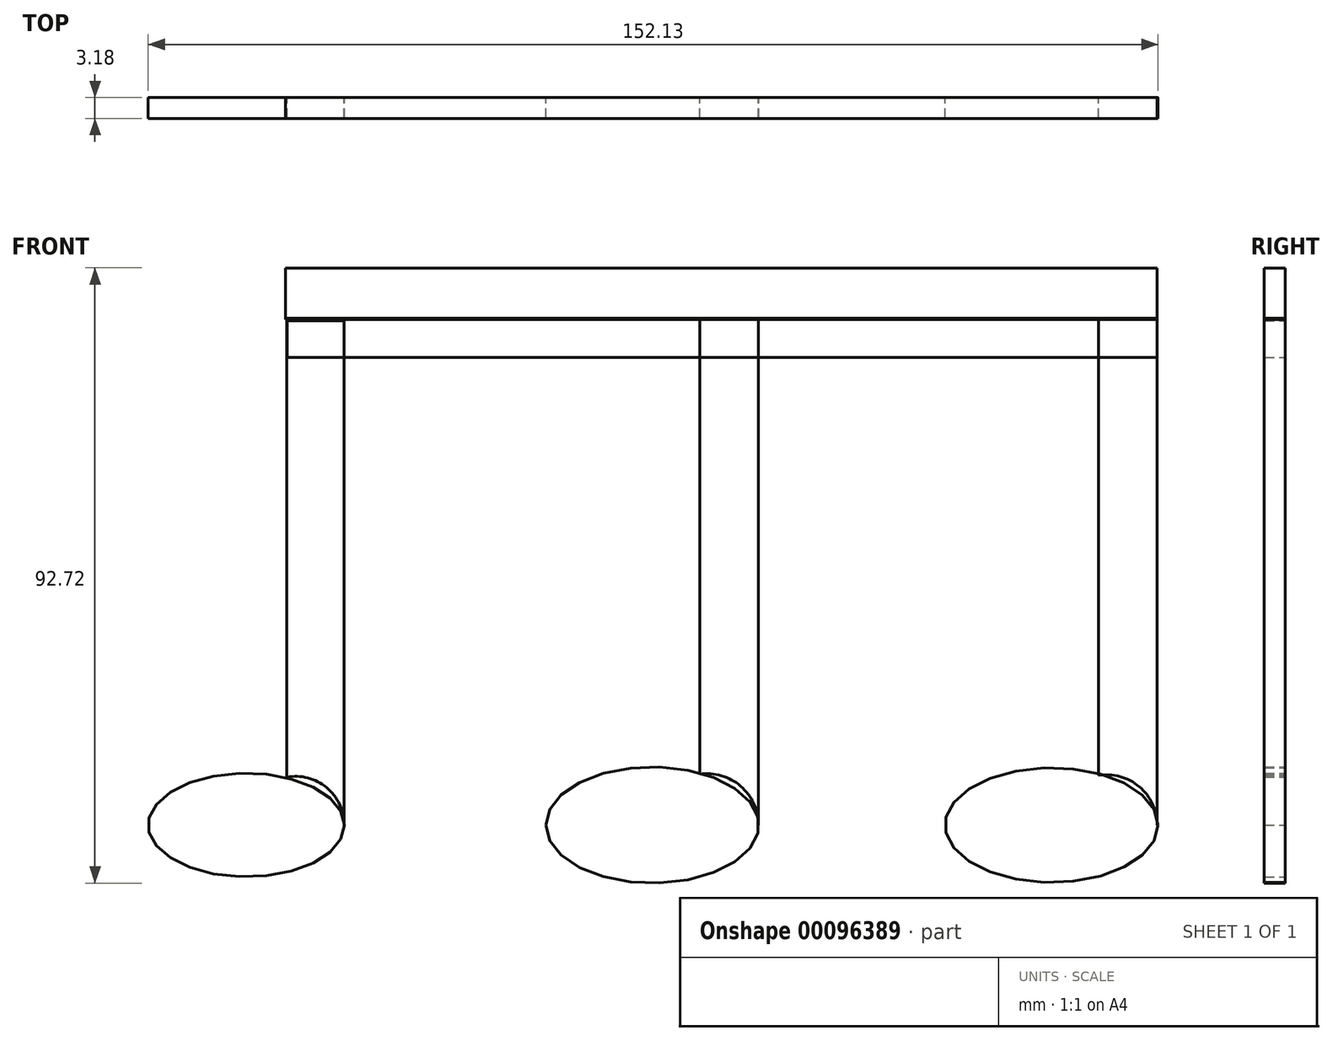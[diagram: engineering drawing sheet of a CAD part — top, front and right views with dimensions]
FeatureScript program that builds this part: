
annotation { "Feature Type Name" : "Feature", "Feature Type Description" : "" }
export const myFeature = defineFeature(function(context is Context, id is Id, definition is map)
    precondition{}
    {
        {
            var Q0;
            Q0=qCreatedBy(makeId("Front.planeOp"),FACE);
            var sketch = newSketch(context, id + "F0", { "sketchPlane" : qUnion([Q0])});
            skEllipse(sketch, "E0", {"center": v(-61.15, 0) * mm, "majorRadius": 14.79 * mm, "minorRadius": 7.8 * mm, "majorAxis": v(1, 0)});
            skSolve(sketch);
        }
        {
            var Q0;
            Q0=qCreatedBy(makeId("Front.planeOp"),FACE);
            var sketch = newSketch(context, id + "F1", { "sketchPlane" : qUnion([Q0])});
            skEllipse(sketch, "E1", {"center": v(60.15, 0) * mm, "majorRadius": 16.04 * mm, "minorRadius": 8.64 * mm, "majorAxis": v(1, 0)});
            skSolve(sketch);
        }
        {
            var Q0;
            Q0=qCreatedBy(makeId("Front.planeOp"),FACE);
            var sketch = newSketch(context, id + "F2", { "sketchPlane" : qUnion([Q0])});
            skEllipse(sketch, "E2", {"center": v(0, 0) * mm, "majorRadius": 16.04 * mm, "minorRadius": 8.75 * mm, "majorAxis": v(-1, 0)});
            skSolve(sketch);
        }
        {
            var Q0;
            Q0=qCreatedBy(makeId("Front.planeOp"),FACE);
            var sketch = newSketch(context, id + "F3", { "sketchPlane" : qUnion([Q0])});
            skLineSegment(sketch, "E3", {"start": v(-46.4, 0) * mm, "end": v(-46.4, 75.98) * mm});
            skLineSegment(sketch, "E4", {"start": v(-46.4, 75.98) * mm, "end": v(-55.1, 75.98) * mm});
            skLineSegment(sketch, "E5", {"start": v(-55.1, 75.98) * mm, "end": v(-55.1, 7.22) * mm});
            skArc(sketch, "E6", {"start": v(-46.4, 0) * mm, "mid": v(-49.06, 5.65) * mm, "end": v(-55.1, 7.22) * mm});
            skSolve(sketch);
        }
        {
            var Q0;
            Q0=qCreatedBy(makeId("Front.planeOp"),FACE);
            var sketch = newSketch(context, id + "F4", { "sketchPlane" : qUnion([Q0])});
            skLineSegment(sketch, "E7", {"start": v(16, 0) * mm, "end": v(16, 76.17) * mm});
            skLineSegment(sketch, "E8", {"start": v(16, 76.17) * mm, "end": v(7.14, 76.17) * mm});
            skLineSegment(sketch, "E9", {"start": v(7.14, 76.17) * mm, "end": v(7.14, 7.67) * mm});
            skArc(sketch, "E10", {"start": v(16, 0) * mm, "mid": v(13.32, 5.86) * mm, "end": v(7.14, 7.67) * mm});
            skSolve(sketch);
        }
        {
            var Q0;
            Q0=qCreatedBy(makeId("Front.planeOp"),FACE);
            var sketch = newSketch(context, id + "F5", { "sketchPlane" : qUnion([Q0])});
            skLineSegment(sketch, "E11", {"start": v(76.06, 0) * mm, "end": v(76.06, 76.38) * mm});
            skLineSegment(sketch, "E12", {"start": v(76.06, 76.38) * mm, "end": v(67.2, 76.38) * mm});
            skLineSegment(sketch, "E13", {"start": v(67.2, 76.38) * mm, "end": v(67.2, 7.46) * mm});
            skArc(sketch, "E14", {"start": v(76.06, 0) * mm, "mid": v(73.36, 5.79) * mm, "end": v(67.2, 7.46) * mm});
            skSolve(sketch);
        }
        {
            var Q0;
            Q0=qCreatedBy(makeId("Front.planeOp"),FACE);
            var sketch = newSketch(context, id + "F6", { "sketchPlane" : qUnion([Q0])});
            skLineSegment(sketch, "E15", {"start": v(-55.25, 76.17) * mm, "end": v(76.06, 76.17) * mm});
            skLineSegment(sketch, "E16", {"start": v(76.06, 76.17) * mm, "end": v(76.06, 83.97) * mm});
            skLineSegment(sketch, "E17", {"start": v(76.06, 83.97) * mm, "end": v(-55.25, 83.97) * mm});
            skLineSegment(sketch, "E18", {"start": v(-55.25, 83.97) * mm, "end": v(-55.25, 76.17) * mm});
            skSolve(sketch);
        }
        {
            var Q0;
            Q0=qCreatedBy(makeId("Front.planeOp"),FACE);
            var sketch = newSketch(context, id + "F7", { "sketchPlane" : qUnion([Q0])});
            skLineSegment(sketch, "E19", {"start": v(-55.02, 70.48) * mm, "end": v(76.04, 70.48) * mm});
            skLineSegment(sketch, "E20", {"start": v(76.04, 70.48) * mm, "end": v(76.04, 76.4) * mm});
            skLineSegment(sketch, "E21", {"start": v(76.04, 76.4) * mm, "end": v(-55.02, 76.4) * mm});
            skLineSegment(sketch, "E22", {"start": v(-55.02, 76.4) * mm, "end": v(-55.02, 70.48) * mm});
            skSolve(sketch);
        }
        {
            var Q0;
            Q0=makeQuery(id+"F0.imprint","IMPRINT",FACE,{"disambiguationData":[TD([[makeQuery(id+"F0.imprint","IMPRINT",EDGE,{"derivedFrom":sQuery(id+"F0.wireOp",EDGE,"E0")}),1.0]])]});
            var Q1;
            Q1=makeQuery(id+"F1.imprint","IMPRINT",FACE,{"disambiguationData":[TD([[makeQuery(id+"F1.imprint","IMPRINT",EDGE,{"derivedFrom":sQuery(id+"F1.wireOp",EDGE,"E1")}),1.0]])]});
            var Q2;
            Q2=makeQuery(id+"F2.imprint","IMPRINT",FACE,{"disambiguationData":[TD([[makeQuery(id+"F2.imprint","IMPRINT",EDGE,{"derivedFrom":sQuery(id+"F2.wireOp",EDGE,"E2")}),1.0]])]});
            var Q3;
            Q3=makeQuery(id+"F3.imprint","IMPRINT",FACE,{"disambiguationData":[TD([[makeQuery(id+"F3.imprint","IMPRINT",EDGE,{"derivedFrom":sQuery(id+"F3.wireOp",EDGE,"E3")}),1.0]])]});
            var Q4;
            Q4=makeQuery(id+"F6.imprint","IMPRINT",FACE,{"disambiguationData":[TD([[makeQuery(id+"F6.imprint","IMPRINT",EDGE,{"derivedFrom":sQuery(id+"F6.wireOp",EDGE,"E15")}),1.0]])]});
            var Q5;
            Q5=makeQuery(id+"F4.imprint","IMPRINT",FACE,{"disambiguationData":[TD([[makeQuery(id+"F4.imprint","IMPRINT",EDGE,{"derivedFrom":sQuery(id+"F4.wireOp",EDGE,"E7")}),1.0]])]});
            var Q6;
            Q6=makeQuery(id+"F5.imprint","IMPRINT",FACE,{"disambiguationData":[TD([[makeQuery(id+"F5.imprint","IMPRINT",EDGE,{"derivedFrom":sQuery(id+"F5.wireOp",EDGE,"E11")}),1.0]])]});
            var Q7;
            Q7=makeQuery(id+"F7.imprint","IMPRINT",FACE,{"disambiguationData":[TD([[makeQuery(id+"F7.imprint","IMPRINT",EDGE,{"derivedFrom":sQuery(id+"F7.wireOp",EDGE,"E19")}),1.0]])]});
            extrude(context, id + "F8", {"entities" : qUnion([Q0, Q1, Q2, Q3, Q4, Q5, Q6, Q7]), "endBound" : BoundingType.SYMMETRIC, "depth" : 3.17 * mm});
        }
    });
